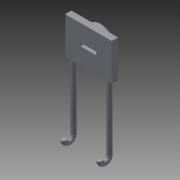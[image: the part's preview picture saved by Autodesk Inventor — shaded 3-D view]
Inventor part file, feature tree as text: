
AUTODESK INVENTOR PART (.ipt)
format: ipt  version: 2015 SP2 (Build 190223200, 223)  size: 142,336 bytes
history: native  units: mm
features: sketch x7, extrude x6, plane x1, revolve x1
ambient origin geometry x8: Origin, YZ Plane, XZ Plane, XY Plane, X Axis, Y Axis, Z Axis, Center Point
bodies: Solid1 (feature_tree)
feature tree (15):
  sketch  "Sketch1"  dims[d0=5.1mm d1=1.0mm]
  sketch  "Sketch2"  dims[d2=15.0mm d3=12.0mm]
  extrude  "Extrusion1"  Depth=1.0mm
  extrude  "Extrusion2"  Depth=12.0mm
  extrude  "Extrusion4"  Depth=2.0mm TaperAngle=0.0deg
  extrude  "Extrusion5"  Depth=4.0mm TaperAngle=0.0deg
  extrude  "Extrusion6"  Depth=5.1mm
  extrude  "Extrusion7"  Depth=3.0mm TaperAngle=0.0deg
  sketch  "Sketch14"  dims[d19=1.5mm d20=21.0mm d21=0.0mm d26=1.5mm d38=360.0deg]
  plane  "Work Plane3"
  revolve  "Revolution1"  [1 undecoded]
  sketch  "Sketch3"  dims[d4=10.0mm d5=2.0mm d6=0.0mm]
  sketch  "Sketch7"  dims[d7=2.0mm d8=0.0mm d11=4.0mm d12=0.0mm]
  sketch  "Sketch8"  dims[d13=3.0mm d14=0.0mm d15=5.1mm]
  sketch  "Sketch9"  dims[d16=1.0mm d17=3.0mm d18=0.0mm]
note: 1 required parameter value undecoded (feature->parameter linkage not recoverable at this tier; creation-order binding heuristic only, values carry confidence <= 0.55)
